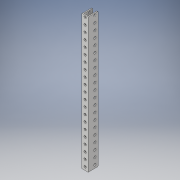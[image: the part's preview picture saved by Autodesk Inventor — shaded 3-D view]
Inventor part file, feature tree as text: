
AUTODESK INVENTOR PART (.ipt)
format: ipt  version: 2017 (Build 210142000, 142)  size: 186,880 bytes
history: native  units: in
note: dims shown in document units (in); Inventor stores cm internally (conversion verified against a paired STEP export)
features: direct_edit x1, fillet x1, move_body x1
ambient origin geometry x8: Origin, YZ Plane, XZ Plane, XY Plane, X Axis, Y Axis, Z Axis, Center Point
bodies: Solid1 (feature_tree)
feature tree (3):
  direct_edit  "Direct Edit3"
  fillet  "Fillet1"  [1 undecoded]
  move_body  "Move3"
note: 1 required parameter value undecoded (feature->parameter linkage not recoverable at this tier; creation-order binding heuristic only, values carry confidence <= 0.55)
